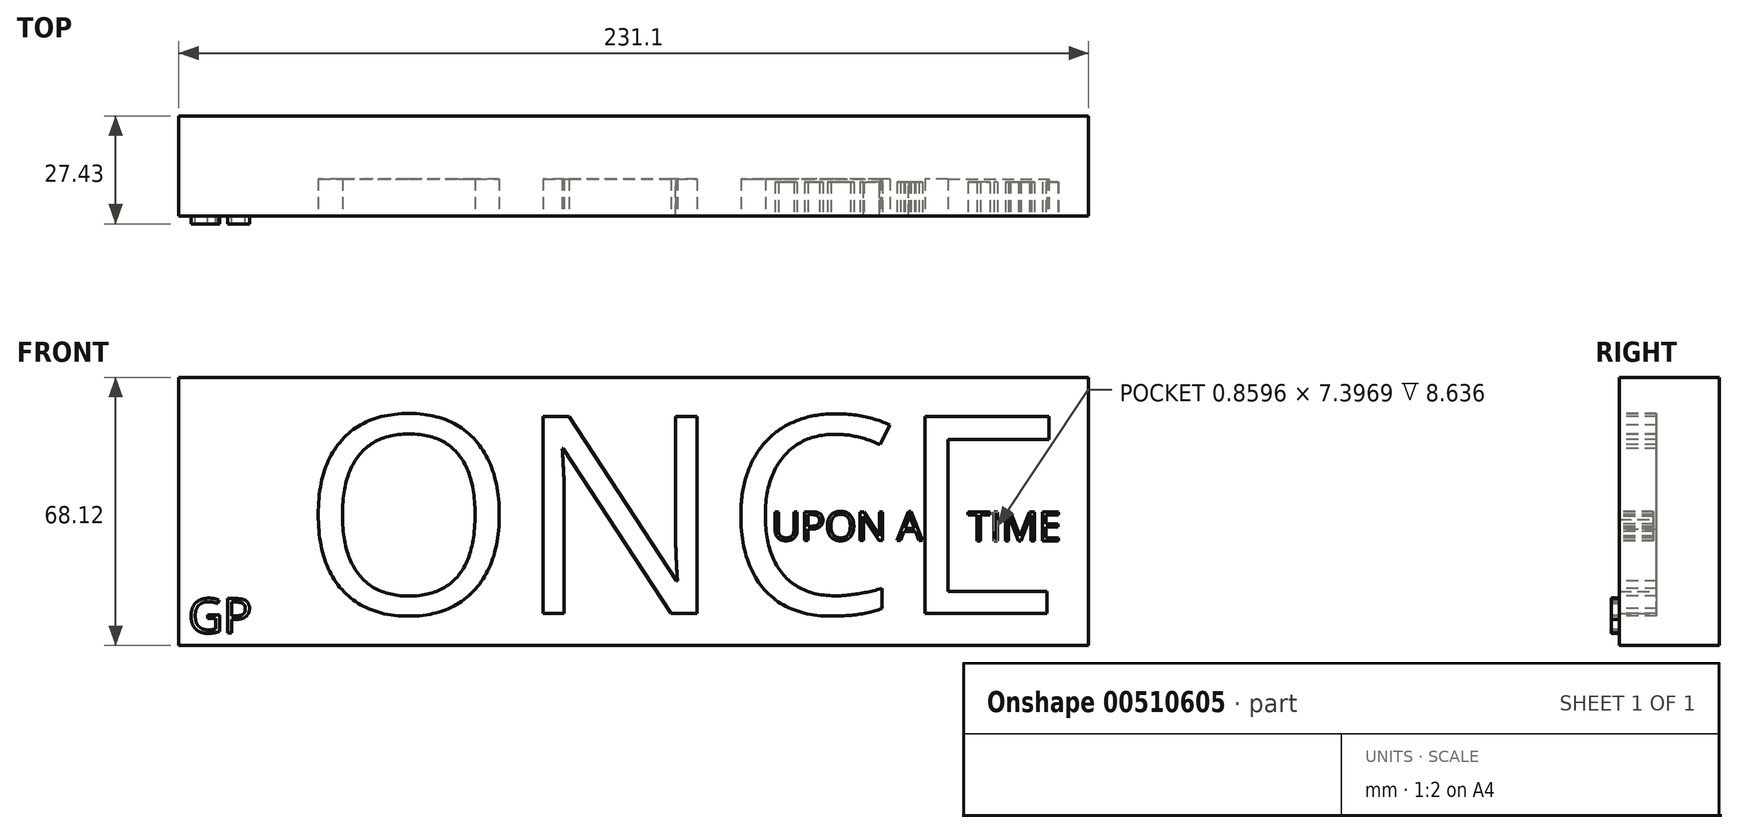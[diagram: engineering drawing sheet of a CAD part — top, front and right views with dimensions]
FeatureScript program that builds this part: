
annotation { "Feature Type Name" : "Feature", "Feature Type Description" : "" }
export const myFeature = defineFeature(function(context is Context, id is Id, definition is map)
    precondition{}
    {
        {
            var Q0;
            Q0=qCreatedBy(makeId("Front.planeOp"),FACE);
            var sketch = newSketch(context, id + "F0", { "sketchPlane" : qUnion([Q0])});
            skLineSegment(sketch, "E0.bottom", {"start": v(115.55, -34.06) * mm, "end": v(-115.55, -34.06) * mm});
            skLineSegment(sketch, "E0.top", {"start": v(115.55, 34.06) * mm, "end": v(-115.55, 34.06) * mm});
            skLineSegment(sketch, "E0.left", {"start": v(115.55, -34.06) * mm, "end": v(115.55, 34.06) * mm});
            skLineSegment(sketch, "E0.right", {"start": v(-115.55, -34.06) * mm, "end": v(-115.55, 34.06) * mm});
            skPoint(sketch, "E0.middle", {"position": v(0, 0) * mm});
            skSolve(sketch);
        }
        {
            var Q0;
            Q0=makeQuery(id+"F0.imprint","IMPRINT",FACE,{"disambiguationData":[TD([[makeQuery(id+"F0.imprint","IMPRINT",EDGE,{"derivedFrom":sQuery(id+"F0.wireOp",EDGE,"E0.bottom")}),-1.0]])]});
            extrude(context, id + "F1", {"entities" : qUnion([Q0]), "depth" : 25.4 * mm, "offsetDistance" : 25.4 * mm});
        }
        {
            var Q0;
            Q0=makeQuery(id+"F1.opExtrude","CAP_FACE",FACE,{"disambiguationData":[OSD([sQuery(id+"F0.wireOp",EDGE,"E0.bottom"),sQuery(id+"F0.wireOp",EDGE,"E0.top"),sQuery(id+"F0.wireOp",EDGE,"E0.left"),sQuery(id+"F0.wireOp",EDGE,"E0.right")])],"isStart":false});
            var sketch = newSketch(context, id + "F2", { "sketchPlane" : qUnion([Q0])});
            skText(sketch, "E1", { "text": "ONCI ", "fontName": "OpenSans-Regular.ttf"});
            const initialGuessF2  = {"E1": [-0.0844, -0.0259, 1, 0, 0.05044]};
            skSetInitialGuess(sketch, initialGuessF2);
            skSolve(sketch);
        }
        {
            var Q0;
            Q0 = qSketchRegion(id + "F2", true);
            extrude(context, id + "F3", {"entities" : qUnion([Q0]), "operationType" : NewBodyOperationType.REMOVE, "oppositeDirection" : true, "depth" : 9.4 * mm, "offsetDistance" : 25.4 * mm});
        }
        {
            var Q0;
            {var subQ0=sQuery(id+"F0.wireOp",EDGE,"E0.left");var subQ1=sQuery(id+"F0.wireOp",EDGE,"E0.bottom");var subQ2=sQuery(id+"F0.wireOp",EDGE,"E0.right");var subQ3=sQuery(id+"F0.wireOp",EDGE,"E0.top");Q0=makeQuery(id+"F3.boolean.opBoolean","SPLIT",FACE,{"disambiguationData":[TD([makeQuery(id+"F1.opExtrude","SWEPT_FACE",FACE,{"disambiguationData":[OSD([subQ1])]})])],"derivedFrom":makeQuery(id+"F1.opExtrude","CAP_FACE",FACE,{"disambiguationData":[OSD([subQ1,subQ3,subQ0,subQ2])],"isStart":false})});}
            var sketch = newSketch(context, id + "F4", { "sketchPlane" : qUnion([Q0])});
            skText(sketch, "E2", { "text": "UPON A", "fontName": "OpenSans-Regular.ttf"});
            const initialGuessF4  = {"E2": [0.03504, -0.00735, 1, 0, 0.00735]};
            skSetInitialGuess(sketch, initialGuessF4);
            skSolve(sketch);
        }
        {
            var Q0;
            Q0 = qSketchRegion(id + "F4", true);
            extrude(context, id + "F5", {"entities" : qUnion([Q0]), "operationType" : NewBodyOperationType.REMOVE, "oppositeDirection" : true, "depth" : 8.64 * mm, "offsetDistance" : 25.4 * mm});
        }
        {
            var Q0;
            {var subQ13=sQuery(id+"F0.wireOp",EDGE,"E0.left");var subQ16=sQuery(id+"F0.wireOp",EDGE,"E0.top");var subQ19=sQuery(id+"F0.wireOp",EDGE,"E0.right");var subQ26=sQuery(id+"F0.wireOp",EDGE,"E0.bottom");var subQ27=makeQuery(id+"F1.opExtrude","SWEPT_FACE",FACE,{"disambiguationData":[OSD([subQ26])]});Q0=makeQuery(id+"F5.boolean.opBoolean","SPLIT",FACE,{"disambiguationData":[TD([subQ27])],"derivedFrom":makeQuery(id+"F3.boolean.opBoolean","SPLIT",FACE,{"disambiguationData":[TD([subQ27])],"derivedFrom":makeQuery(id+"F1.opExtrude","CAP_FACE",FACE,{"disambiguationData":[OSD([subQ26,subQ16,subQ13,subQ19])],"isStart":false})})});}
            var sketch = newSketch(context, id + "F6", { "sketchPlane" : qUnion([Q0])});
            skText(sketch, "E3", { "text": "TIME", "fontName": "OpenSans-Regular.ttf"});
            const initialGuessF6  = {"E3": [0.08485, -0.00746, 1, 0, 0.00746]};
            skSetInitialGuess(sketch, initialGuessF6);
            skSolve(sketch);
        }
        {
            var Q0;
            Q0 = qSketchRegion(id + "F6", true);
            extrude(context, id + "F7", {"entities" : qUnion([Q0]), "operationType" : NewBodyOperationType.REMOVE, "oppositeDirection" : true, "depth" : 8.64 * mm, "offsetDistance" : 25.4 * mm});
        }
        {
            var Q0;
            {var subQ13=sQuery(id+"F0.wireOp",EDGE,"E0.left");var subQ16=sQuery(id+"F0.wireOp",EDGE,"E0.top");var subQ19=sQuery(id+"F0.wireOp",EDGE,"E0.right");var subQ26=sQuery(id+"F0.wireOp",EDGE,"E0.bottom");var subQ27=makeQuery(id+"F1.opExtrude","SWEPT_FACE",FACE,{"disambiguationData":[OSD([subQ26])]});Q0=makeQuery(id+"F5.boolean.opBoolean","SPLIT",FACE,{"disambiguationData":[TD([subQ27])],"derivedFrom":makeQuery(id+"F3.boolean.opBoolean","SPLIT",FACE,{"disambiguationData":[TD([subQ27])],"derivedFrom":makeQuery(id+"F1.opExtrude","CAP_FACE",FACE,{"disambiguationData":[OSD([subQ26,subQ16,subQ13,subQ19])],"isStart":false})})});}
            var sketch = newSketch(context, id + "F8", { "sketchPlane" : qUnion([Q0])});
            skLineSegment(sketch, "E4.bottom", {"start": v(79.86, 24.12) * mm, "end": v(105.48, 24.12) * mm});
            skLineSegment(sketch, "E4.top", {"start": v(79.86, 18.34) * mm, "end": v(105.48, 18.34) * mm});
            skLineSegment(sketch, "E4.left", {"start": v(79.86, 24.12) * mm, "end": v(79.86, 18.34) * mm});
            skLineSegment(sketch, "E4.right", {"start": v(105.48, 24.12) * mm, "end": v(105.48, 18.34) * mm});
            skLineSegment(sketch, "E5.bottom", {"start": v(79.86, -25.9) * mm, "end": v(105.07, -25.9) * mm});
            skLineSegment(sketch, "E5.top", {"start": v(79.86, -20.35) * mm, "end": v(105.07, -20.35) * mm});
            skLineSegment(sketch, "E5.left", {"start": v(79.86, -25.9) * mm, "end": v(79.86, -20.35) * mm});
            skLineSegment(sketch, "E5.right", {"start": v(105.07, -25.9) * mm, "end": v(105.07, -20.35) * mm});
            skSolve(sketch);
        }
        {
            var Q0;
            Q0=makeQuery(id+"F8.imprint","IMPRINT",FACE,{"disambiguationData":[TD([[makeQuery(id+"F8.imprint","IMPRINT",EDGE,{"derivedFrom":sQuery(id+"F8.wireOp",EDGE,"E4.bottom")}),-1.0]])]});
            var Q1;
            Q1=makeQuery(id+"F8.imprint","IMPRINT",FACE,{"disambiguationData":[TD([[makeQuery(id+"F8.imprint","IMPRINT",EDGE,{"derivedFrom":sQuery(id+"F8.wireOp",EDGE,"E5.bottom")}),1.0]])]});
            extrude(context, id + "F9", {"entities" : qUnion([Q0, Q1]), "operationType" : NewBodyOperationType.REMOVE, "oppositeDirection" : true, "depth" : 9.4 * mm, "offsetDistance" : 25.4 * mm});
        }
        {
            var Q0;
            {var subQ13=sQuery(id+"F0.wireOp",EDGE,"E0.left");var subQ16=sQuery(id+"F0.wireOp",EDGE,"E0.top");var subQ19=sQuery(id+"F0.wireOp",EDGE,"E0.right");var subQ26=sQuery(id+"F0.wireOp",EDGE,"E0.bottom");var subQ27=makeQuery(id+"F1.opExtrude","SWEPT_FACE",FACE,{"disambiguationData":[OSD([subQ26])]});Q0=makeQuery(id+"F5.boolean.opBoolean","SPLIT",FACE,{"disambiguationData":[TD([subQ27])],"derivedFrom":makeQuery(id+"F3.boolean.opBoolean","SPLIT",FACE,{"disambiguationData":[TD([subQ27])],"derivedFrom":makeQuery(id+"F1.opExtrude","CAP_FACE",FACE,{"disambiguationData":[OSD([subQ26,subQ16,subQ13,subQ19])],"isStart":false})})});}
            var sketch = newSketch(context, id + "F10", { "sketchPlane" : qUnion([Q0])});
            skText(sketch, "E6", { "text": "GP", "fontName": "OpenSans-Regular.ttf"});
            const initialGuessF10  = {"E6": [-0.11318, -0.03084, 1, 0, 0.00878]};
            skSetInitialGuess(sketch, initialGuessF10);
            skSolve(sketch);
        }
        {
            var Q0;
            Q0 = qSketchRegion(id + "F10", true);
            extrude(context, id + "F11", {"entities" : qUnion([Q0]), "operationType" : NewBodyOperationType.ADD, "depth" : 2.03 * mm, "offsetDistance" : 25.4 * mm});
        }
    });
